# Revit family: Tyco_Fire Detector_and_Alarm Control_Indicator_Equipment-Profile Flexible Addressable _Control and Indicating Panels
name_source: partatom
category: Fire Alarm Devices
revit_build: Autodesk Revit 2014 (Build: 20130308_1515(x64)
units: mm (PartAtom-declared; Revit-internal decimal feet)

## types (5) — shared parameters
Asset Type = Moveable
Brand = Zettler
Colour = RAL 7016 (Anthracite Grey) & RAL 7040 (Window Grey)
Default Elevation = 1219 mm
Manufacturer = Tyco Fire Protection Products
Manufacturer URL = www.zettlerfire.com
Material = Mild steel Zintec (Electro Zinc Coated)
Nominal Length = 263 mm  [stored 0.862861 ft]
Nominal Width = 438 mm  [stored 1.43701 ft]
Operation Temperature Range = -8 °C to +55 °C
Relative Humidity = 90% RH continuous (non-condensing)
Shape = Rectangle
Storage Temperature = -20 °C to +70 °C
URL = http://www.zettlerfire.com
Warranty Duration Labor = 1.5
Warranty Duration Parts = 1.5
Warranty Duration Unit = Year
zero-valued in all types: Expected Life, Replacement Cost

## per-type parameters (varying)
| type | Clearance ref | Description | Display A | Display B | Geometry ref | Model | Model Number | Nominal Height | Product Codes |
| Pro16xD 4-16 Loop PROFILE Panel | 0 mm  [stored 0 ft] | Pro16xD PROFILE flexible panel 4 Shared Power Loops or 2 High Power Loops. Expandable to 16 Shared Power Loops or 8 High Power Loops max 2000 addresses. TFT touchscreen display, 5A PSU deep XL housing for 38 AH batteries supplied with mounting frame. | Yes | No | No | Pro16xD | Pro16xD | 480 mm  [stored 1.5748 ft] | 557.200.847 |
| Pro16xBB 4-16 Loop PROFILE Black Box | 0 mm  [stored 0 ft] | Pro16xBB PROFILE flexible Black Box panel 4 Shared Power Loops or 2 High Power Loops. Expandable to 16 Shared Power Loops or 8 High Power Loops max 2000 addresses, 5A PSU deep XL housing for 38 AH batteries supplied with mounting frame. | No | Yes | No | Pro16xBB | Pro16xBB | 480 mm  [stored 1.5748 ft] | 557.200.850 |
| Pro32xD 4-32 Loop PROFILE Panel | 246 mm  [stored 0.807087 ft] | Pro32xD PROFILE flexible panel 4 Shared Power Loops or 2 High Power Loops. Expandable to 32 Shared Power Loops or 16 High Power Loops max 2000 addresses. TFT touchscreen display, XL housing supplied with mounting frame. | Yes | No | Yes | Pro32xD | Pro32xD | 740 mm  [stored 2.42782 ft] | 557.200.848 |
| Pro32xBB 4-32 Loop PROFILE Black Box | 246 mm  [stored 0.807087 ft] | Pro32xBB PROFILE flexible Black Box panel 4 Shared Power Loops or 2 High Power Loops. Expandable to 32 Shared Power Loops or 16 High Power Loops max 2000 addresses. XL housing supplied with mounting frame. | No | Yes | Yes | Pro32xBB | Pro32xBB | 740 mm  [stored 2.42782 ft] | 557.200.851 |
| PxD Extension Box For Pro32xD | 0 mm  [stored 0 ft] | PxD Extension box for Pro32xD PROFILE Flexible panel to enable a maximum number of 32 SP-loops, 4000 addresses XL housing with 6 way slot card cage and space for a second six way slot card cage. Supplied with mounting frame. | No | No | No | PxD | PxD | 480 mm  [stored 1.5748 ft] | 557.200.849 |

note: column(s) folded — value = type name in every type: Name, Product Specification

note: [stored X ft] marks values corroborated as IEEE doubles in the binary element streams (Revit-internal decimal feet)

## geometry (parser evidence)
native form markers: Sweep x12
no freeform markers — native parametric forms only
